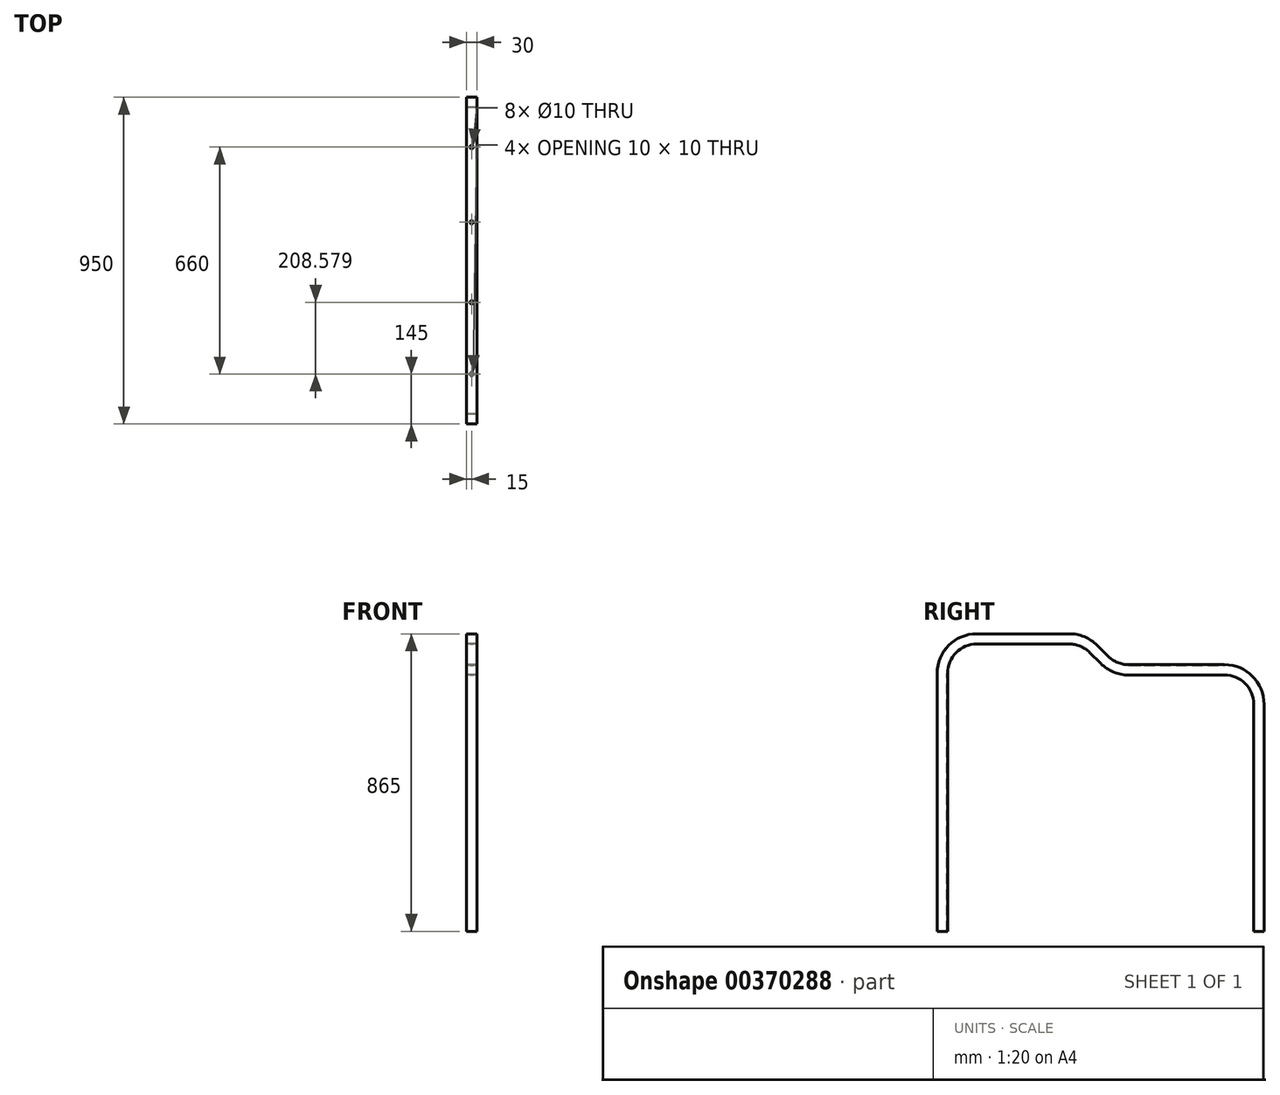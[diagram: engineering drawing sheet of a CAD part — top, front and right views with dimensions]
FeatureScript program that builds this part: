
annotation { "Feature Type Name" : "Feature", "Feature Type Description" : "" }
export const myFeature = defineFeature(function(context is Context, id is Id, definition is map)
    precondition{}
    {
        {
            var Q0;
            Q0=qCreatedBy(makeId("Right.planeOp"),FACE);
            var sketch = newSketch(context, id + "F0", { "sketchPlane" : qUnion([Q0])});
            skLineSegment(sketch, "E0", {"start": v(0, 0) * mm, "end": v(0, 750) * mm});
            skLineSegment(sketch, "E1", {"start": v(100, 850) * mm, "end": v(368.58, 850) * mm});
            skLineSegment(sketch, "E2", {"start": v(439.29, 820.71) * mm, "end": v(470.71, 789.29) * mm});
            skLineSegment(sketch, "E3", {"start": v(541.42, 760) * mm, "end": v(820, 760) * mm});
            skLineSegment(sketch, "E4", {"start": v(920, 660) * mm, "end": v(920, 0) * mm});
            skPoint(sketch, "E5.visualSharp", {"position": v(0, 850) * mm});
            skArc(sketch, "E5.filletArc", {"start": v(100, 850) * mm, "mid": v(29.29, 820.71) * mm, "end": v(0, 750) * mm});
            skPoint(sketch, "E6.visualSharp", {"position": v(920, 760) * mm});
            skArc(sketch, "E6.filletArc", {"start": v(920, 660) * mm, "mid": v(890.71, 730.71) * mm, "end": v(820, 760) * mm});
            skPoint(sketch, "E7.visualSharp", {"position": v(410, 850) * mm});
            skArc(sketch, "E7.filletArc", {"start": v(439.29, 820.71) * mm, "mid": v(406.85, 842.39) * mm, "end": v(368.58, 850) * mm});
            skPoint(sketch, "E8.visualSharp", {"position": v(500, 760) * mm});
            skArc(sketch, "E8.filletArc", {"start": v(470.71, 789.29) * mm, "mid": v(503.15, 767.61) * mm, "end": v(541.42, 760) * mm});
            skSolve(sketch);
        }
        {
            var Q0;
            Q0=qCreatedBy(makeId("Top.planeOp"),FACE);
            var sketch = newSketch(context, id + "F1", { "sketchPlane" : qUnion([Q0])});
            skLineSegment(sketch, "E9.bottom", {"start": v(15, 15) * mm, "end": v(-15, 15) * mm});
            skLineSegment(sketch, "E9.top", {"start": v(15, -15) * mm, "end": v(-15, -15) * mm});
            skLineSegment(sketch, "E9.left", {"start": v(15, 15) * mm, "end": v(15, -15) * mm});
            skLineSegment(sketch, "E9.right", {"start": v(-15, 15) * mm, "end": v(-15, -15) * mm});
            skPoint(sketch, "E9.middle", {"position": v(0, 0) * mm});
            skLineSegment(sketch, "E10.bottom", {"start": v(13.5, 13.5) * mm, "end": v(-13.5, 13.5) * mm});
            skLineSegment(sketch, "E10.top", {"start": v(13.5, -13.5) * mm, "end": v(-13.5, -13.5) * mm});
            skLineSegment(sketch, "E10.left", {"start": v(13.5, 13.5) * mm, "end": v(13.5, -13.5) * mm});
            skLineSegment(sketch, "E10.right", {"start": v(-13.5, 13.5) * mm, "end": v(-13.5, -13.5) * mm});
            skSolve(sketch);
        }
        {
            var Q0;
            Q0=makeQuery(id+"F1.imprint","IMPRINT",FACE,{"disambiguationData":[TD([[makeQuery(id+"F1.imprint","IMPRINT",EDGE,{"derivedFrom":sQuery(id+"F1.wireOp",EDGE,"E9.bottom")}),1.0]])]});
            var Q1;
            Q1 = qConstructionFilter(qBodyType(qCreatedBy(id + "F0" ,EDGE), BodyType.WIRE), ConstructionObject.NO);
            sweep(context, id + "F2", {"profiles" : qUnion([Q0]), "path" : qUnion([Q1])});
        }
        {
            var Q0;
            Q0=makeQuery(id+"F2.opSweep","SWEPT_FACE",FACE,{"disambiguationData":[OSD([sQuery(id+"F0.wireOp",EDGE,"E1"),sQuery(id+"F1.wireOp",EDGE,"E9.top")])]});
            var sketch = newSketch(context, id + "F3", { "sketchPlane" : qUnion([Q0])});
            skCircle(sketch, "E11", {"center": v(0, 130) * mm, "radius": 5 * mm});
            skPoint(sketch, "E11.centerSnap0", {"position": v(0, 100) * mm});
            skCircle(sketch, "E12", {"center": v(0, 338.58) * mm, "radius": 5 * mm});
            skSolve(sketch);
        }
        {
            var Q0;
            Q0=makeQuery(id+"F2.opSweep","SWEPT_FACE",FACE,{"disambiguationData":[OSD([sQuery(id+"F0.wireOp",EDGE,"E3"),sQuery(id+"F1.wireOp",EDGE,"E9.top")])]});
            var sketch = newSketch(context, id + "F4", { "sketchPlane" : qUnion([Q0])});
            skCircle(sketch, "E13", {"center": v(0, 571.42) * mm, "radius": 5 * mm});
            skPoint(sketch, "E13.centerSnap0", {"position": v(0, 541.42) * mm});
            skCircle(sketch, "E14", {"center": v(0, 790) * mm, "radius": 5 * mm});
            skSolve(sketch);
        }
        {
            var Q0;
            Q0 = qSketchRegion(id + "F3", true);
            extrude(context, id + "F5", {"entities" : qUnion([Q0]), "operationType" : NewBodyOperationType.REMOVE, "oppositeDirection" : true, "depth" : 40 * mm});
        }
        {
            var Q0;
            Q0 = qSketchRegion(id + "F4", true);
            extrude(context, id + "F6", {"entities" : qUnion([Q0]), "operationType" : NewBodyOperationType.REMOVE, "oppositeDirection" : true, "depth" : 40 * mm});
        }
    });
